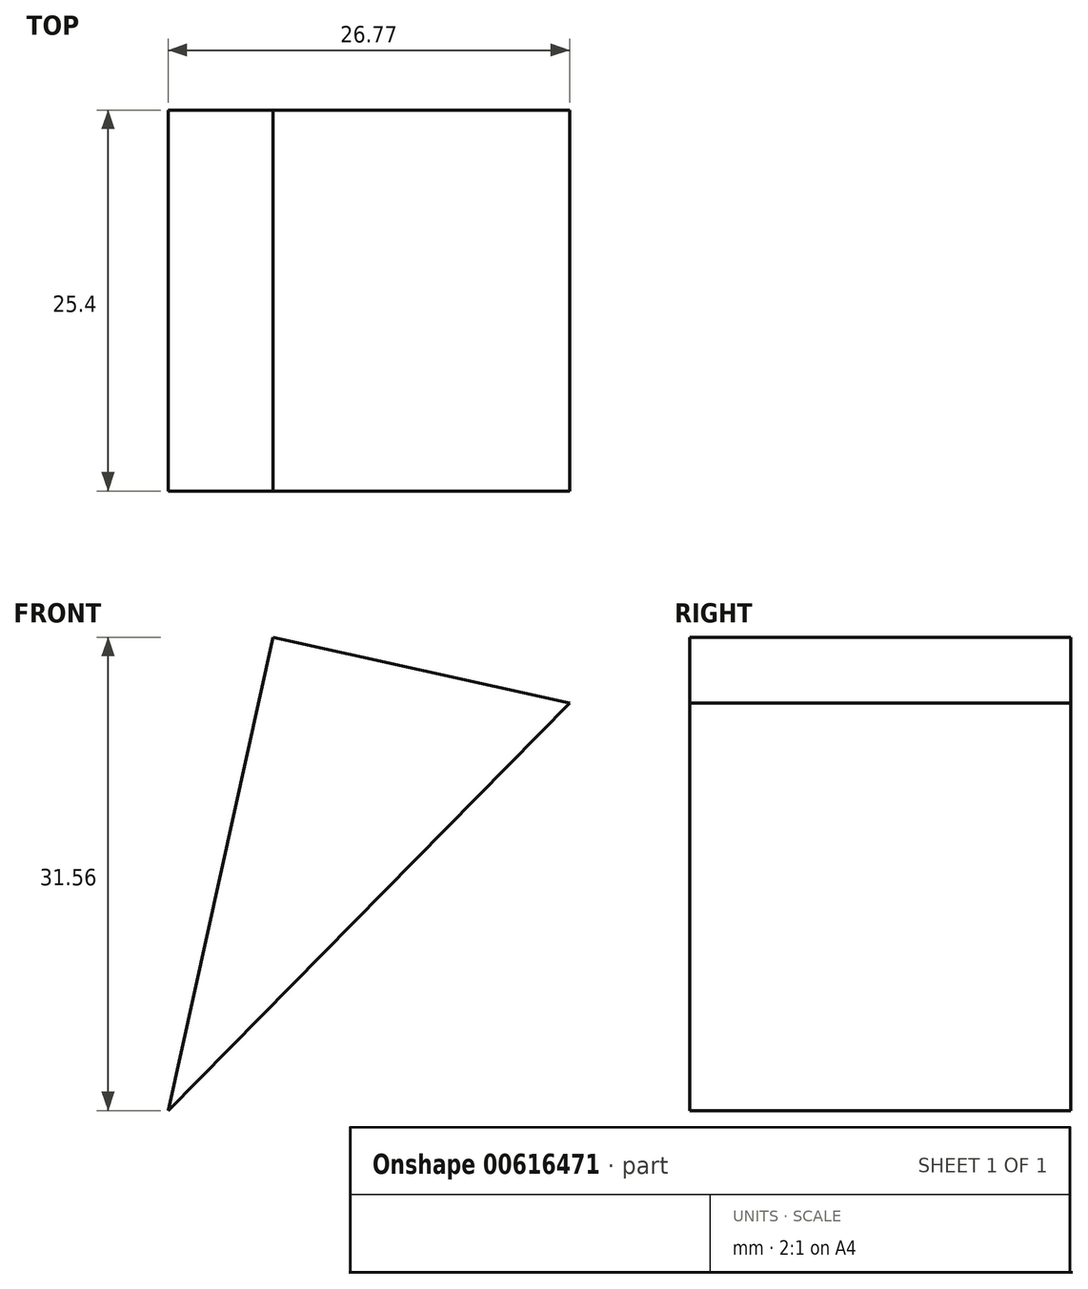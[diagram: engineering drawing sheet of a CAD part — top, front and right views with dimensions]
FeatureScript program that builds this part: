
annotation { "Feature Type Name" : "Feature", "Feature Type Description" : "" }
export const myFeature = defineFeature(function(context is Context, id is Id, definition is map)
    precondition{}
    {
        {
            var Q0;
            Q0=qCreatedBy(makeId("Front.planeOp"),FACE);
            var sketch = newSketch(context, id + "F0", { "sketchPlane" : qUnion([Q0])});
            skLineSegment(sketch, "E0", {"start": v(51.64, 49.38) * mm, "end": v(31.85, 53.76) * mm});
            skLineSegment(sketch, "E1", {"start": v(31.85, 53.76) * mm, "end": v(24.87, 22.2) * mm});
            skLineSegment(sketch, "E2", {"start": v(24.87, 22.2) * mm, "end": v(51.64, 49.38) * mm});
            skSolve(sketch);
        }
        {
            var Q0;
            Q0 = qSketchRegion(id + "F0", true);
            extrude(context, id + "F1", {"entities" : qUnion([Q0]), "endBound" : BoundingType.SYMMETRIC, "depth" : 25.4 * mm, "offsetDistance" : 25.4 * mm});
        }
    });
